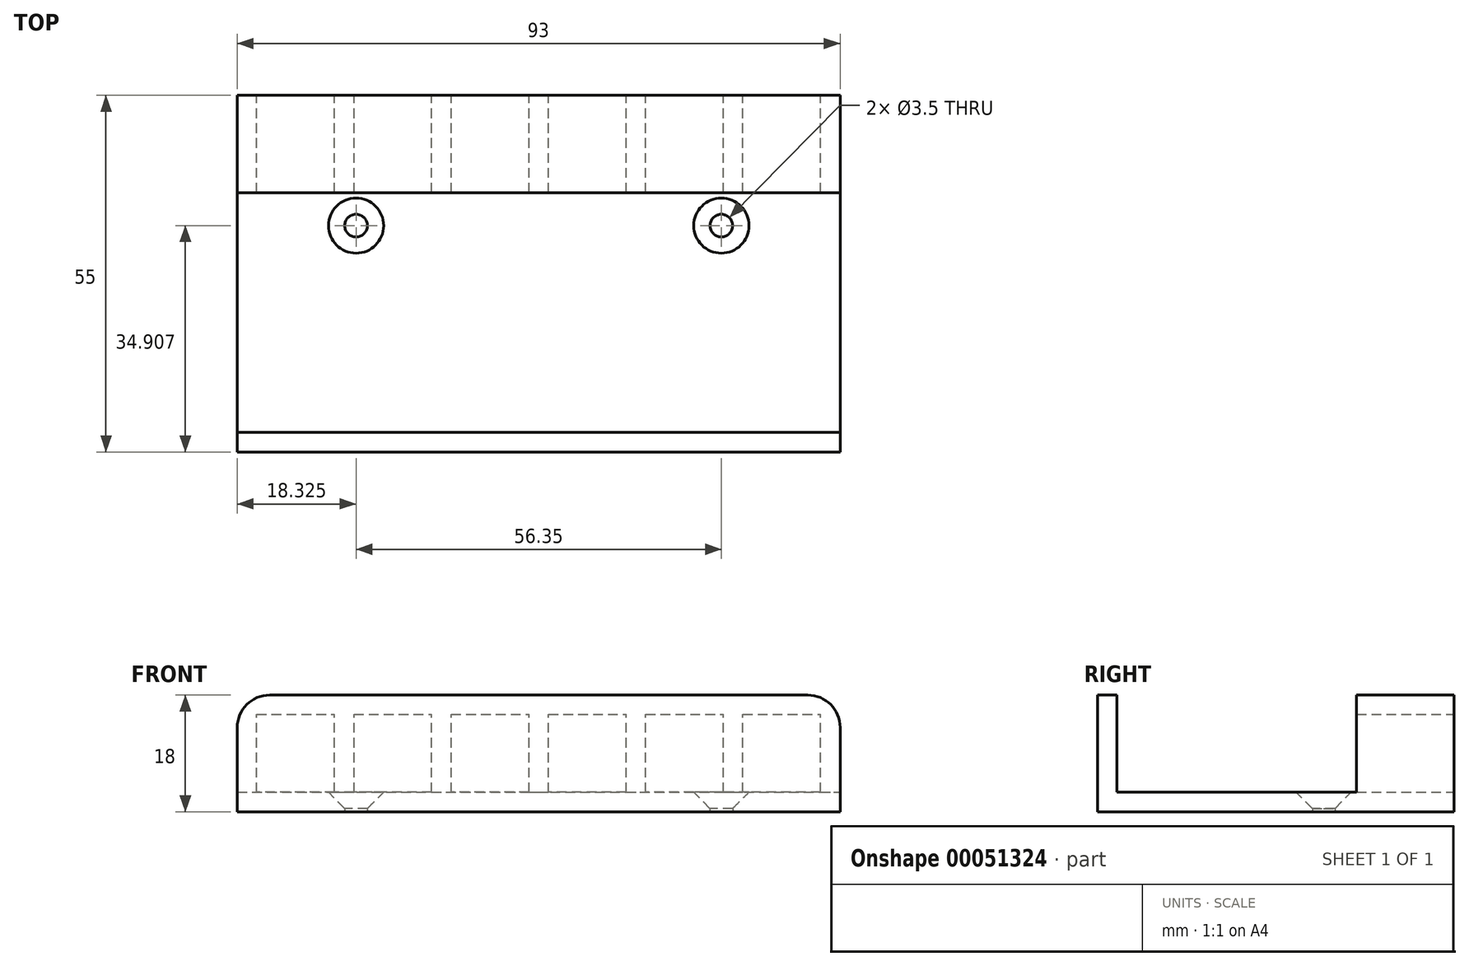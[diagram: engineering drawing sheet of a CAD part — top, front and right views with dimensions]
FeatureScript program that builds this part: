
annotation { "Feature Type Name" : "Feature", "Feature Type Description" : "" }
export const myFeature = defineFeature(function(context is Context, id is Id, definition is map)
    precondition{}
    {
        {
            var Q0;
            Q0=qCreatedBy(makeId("Top.planeOp"),FACE);
            var sketch = newSketch(context, id + "F0", { "sketchPlane" : qUnion([Q0])});
            skLineSegment(sketch, "E0.bottom", {"start": v(0, 0) * mm, "end": v(93, 0) * mm});
            skLineSegment(sketch, "E0.top", {"start": v(0, 55) * mm, "end": v(93, 55) * mm});
            skLineSegment(sketch, "E0.left", {"start": v(0, 0) * mm, "end": v(0, 55) * mm});
            skLineSegment(sketch, "E0.right", {"start": v(93, 0) * mm, "end": v(93, 55) * mm});
            skCircle(sketch, "E1", {"center": v(18.33, 34.9) * mm, "radius": 1.75 * mm});
            skCircle(sketch, "E2", {"center": v(74.67, 34.9) * mm, "radius": 1.75 * mm});
            skLineSegment(sketch, "E3", {"start": v(46.5, 55) * mm, "end": v(46.5, 0) * mm, "construction": true});
            skSolve(sketch);
        }
        {
            var Q0;
            Q0 = qSketchRegion(id + "F0", true);
            extrude(context, id + "F1", {"entities" : qUnion([Q0]), "depth" : 3 * mm});
        }
        {
            var Q0;
            Q0=makeQuery(id+"F1.opExtrude","CAP_FACE",FACE,{"disambiguationData":[OSD([sQuery(id+"F0.wireOp",EDGE,"E0.bottom"),sQuery(id+"F0.wireOp",EDGE,"E0.top"),sQuery(id+"F0.wireOp",EDGE,"E0.left"),sQuery(id+"F0.wireOp",EDGE,"E0.right"),sQuery(id+"F0.wireOp",EDGE,"E1"),sQuery(id+"F0.wireOp",EDGE,"E2")])],"isStart":false});
            var sketch = newSketch(context, id + "F2", { "sketchPlane" : qUnion([Q0])});
            skLineSegment(sketch, "E4.bottom", {"start": v(0, 0) * mm, "end": v(93, 0) * mm});
            skLineSegment(sketch, "E4.top", {"start": v(0, 3) * mm, "end": v(93, 3) * mm});
            skLineSegment(sketch, "E4.left", {"start": v(0, 0) * mm, "end": v(0, 3) * mm});
            skLineSegment(sketch, "E4.right", {"start": v(93, 0) * mm, "end": v(93, 3) * mm});
            skLineSegment(sketch, "E5.bottom", {"start": v(0, 55) * mm, "end": v(93, 55) * mm});
            skLineSegment(sketch, "E5.top", {"start": v(0, 40) * mm, "end": v(93, 40) * mm});
            skLineSegment(sketch, "E5.left", {"start": v(0, 55) * mm, "end": v(0, 40) * mm});
            skLineSegment(sketch, "E5.right", {"start": v(93, 55) * mm, "end": v(93, 40) * mm});
            skSolve(sketch);
        }
        {
            var Q0;
            Q0 = qSketchRegion(id + "F2", true);
            extrude(context, id + "F3", {"entities" : qUnion([Q0]), "operationType" : NewBodyOperationType.ADD, "depth" : 15 * mm});
        }
        {
            var Q0;
            Q0=makeQuery(id+"F3.boolean.opBoolean","MERGE",FACE,{"derivedFrom":[makeQuery(id+"F1.opExtrude","SWEPT_FACE",FACE,{"disambiguationData":[OSD([sQuery(id+"F0.wireOp",EDGE,"E0.top")])]}),makeQuery(id+"F3.opExtrude","SWEPT_FACE",FACE,{"disambiguationData":[OSD([sQuery(id+"F2.wireOp",EDGE,"E5.bottom")])]})]});
            var sketch = newSketch(context, id + "F4", { "sketchPlane" : qUnion([Q0])});
            skLineSegment(sketch, "E6.bottom", {"start": v(-90, 15) * mm, "end": v(-78, 15) * mm});
            skLineSegment(sketch, "E6.top", {"start": v(-90, 3) * mm, "end": v(-78, 3) * mm});
            skLineSegment(sketch, "E6.left", {"start": v(-90, 15) * mm, "end": v(-90, 3) * mm});
            skLineSegment(sketch, "E6.right", {"start": v(-78, 15) * mm, "end": v(-78, 3) * mm});
            skLineSegment(sketch, "E7.1.0.0", {"start": v(-75, 15) * mm, "end": v(-63, 15) * mm});
            skLineSegment(sketch, "E7.1.0.1", {"start": v(-75, 15) * mm, "end": v(-75, 3) * mm});
            skLineSegment(sketch, "E7.1.0.2", {"start": v(-75, 3) * mm, "end": v(-63, 3) * mm});
            skLineSegment(sketch, "E7.1.0.3", {"start": v(-63, 15) * mm, "end": v(-63, 3) * mm});
            skLineSegment(sketch, "E7.2.0.0", {"start": v(-60, 15) * mm, "end": v(-48, 15) * mm});
            skLineSegment(sketch, "E7.2.0.1", {"start": v(-60, 15) * mm, "end": v(-60, 3) * mm});
            skLineSegment(sketch, "E7.2.0.2", {"start": v(-60, 3) * mm, "end": v(-48, 3) * mm});
            skLineSegment(sketch, "E7.2.0.3", {"start": v(-48, 15) * mm, "end": v(-48, 3) * mm});
            skLineSegment(sketch, "E7.3.0.0", {"start": v(-45, 15) * mm, "end": v(-33, 15) * mm});
            skLineSegment(sketch, "E7.3.0.1", {"start": v(-45, 15) * mm, "end": v(-45, 3) * mm});
            skLineSegment(sketch, "E7.3.0.2", {"start": v(-45, 3) * mm, "end": v(-33, 3) * mm});
            skLineSegment(sketch, "E7.3.0.3", {"start": v(-33, 15) * mm, "end": v(-33, 3) * mm});
            skLineSegment(sketch, "E7.4.0.0", {"start": v(-30, 15) * mm, "end": v(-18, 15) * mm});
            skLineSegment(sketch, "E7.4.0.1", {"start": v(-30, 15) * mm, "end": v(-30, 3) * mm});
            skLineSegment(sketch, "E7.4.0.2", {"start": v(-30, 3) * mm, "end": v(-18, 3) * mm});
            skLineSegment(sketch, "E7.4.0.3", {"start": v(-18, 15) * mm, "end": v(-18, 3) * mm});
            skLineSegment(sketch, "E7.5.0.0", {"start": v(-15, 15) * mm, "end": v(-3, 15) * mm});
            skLineSegment(sketch, "E7.5.0.1", {"start": v(-15, 15) * mm, "end": v(-15, 3) * mm});
            skLineSegment(sketch, "E7.5.0.2", {"start": v(-15, 3) * mm, "end": v(-3, 3) * mm});
            skLineSegment(sketch, "E7.5.0.3", {"start": v(-3, 15) * mm, "end": v(-3, 3) * mm});
            skLineSegment(sketch, "E7.direction1", {"start": v(-90, 15) * mm, "end": v(-75, 15) * mm, "construction": true});
            skSolve(sketch);
        }
        {
            var Q0;
            Q0 = qSketchRegion(id + "F4", true);
            extrude(context, id + "F5", {"entities" : qUnion([Q0]), "operationType" : NewBodyOperationType.REMOVE, "endBound" : BoundingType.UP_TO_NEXT, "oppositeDirection" : true, "depth" : 25 * mm});
        }
        {
            var Q0;
            Q0=makeQuery(id+"F1.opExtrude","CAP_EDGE",EDGE,{"disambiguationData":[OSD([sQuery(id+"F0.wireOp",EDGE,"E1")])],"isStart":false});
            var Q1;
            Q1=makeQuery(id+"F1.opExtrude","CAP_EDGE",EDGE,{"disambiguationData":[OSD([sQuery(id+"F0.wireOp",EDGE,"E2")])],"isStart":false});
            chamfer(context, id + "F6", {"entities" : qUnion([Q0, Q1]), "width" : 2.5 * mm, "tangentPropagation" : true});
        }
        {
            var Q0;
            Q0=makeQuery(id+"F3.opExtrude","CAP_EDGE",EDGE,{"disambiguationData":[OSD([sQuery(id+"F2.wireOp",EDGE,"E5.left")])],"isStart":false});
            var Q1;
            Q1=makeQuery(id+"F3.opExtrude","CAP_EDGE",EDGE,{"disambiguationData":[OSD([sQuery(id+"F2.wireOp",EDGE,"E5.right")])],"isStart":false});
            var Q2;
            Q2=makeQuery(id+"F3.opExtrude","CAP_EDGE",EDGE,{"disambiguationData":[OSD([sQuery(id+"F2.wireOp",EDGE,"E4.right")])],"isStart":false});
            var Q3;
            Q3=makeQuery(id+"F3.opExtrude","CAP_EDGE",EDGE,{"disambiguationData":[OSD([sQuery(id+"F2.wireOp",EDGE,"E4.left")])],"isStart":false});
            fillet(context, id + "F7", {"entities" : qUnion([Q0, Q1, Q2, Q3]), "radius" : 5 * mm, "tangentPropagation" : true, "allowEdgeOverflow" : false});
        }
    });
